# Revit family: 57_CRD_ME_Vita_H1C
name_source: partatom
category: Mechanical Equipment
units: mm (PartAtom-declared; Revit-internal decimal feet)

## family parameters
Always vertical = Yes
Classification = None
Cut with Voids When Loaded = Yes
Part Type = Normal
Room Calculation Point = Yes
Round Connector Dimension = Use Diameter
Shared = No
Work Plane-Based = Yes

## types (1)
- 1320  x 485 x 142
    Default Elevation = 1219 mm
    Description = ClimaRad Sensa H2X ventilatie-unit
    Manufacturer = ClimaRad
    Model = Sensa H2X
    bk_ril = 305 mm  [stored 1.00066 ft]
    borstwering = 465 mm  [stored 1.52559 ft]
    diepte = 270 mm  [stored 0.885827 ft]
    diepte_achterpaneel = 70 mm  [stored 0.229659 ft]
    diepte_ril = 6 mm  [stored 0.019685 ft]
    hart_doorvoer_tov_ok_kast = 345 mm  [stored 1.13189 ft]
    hart_wcd_tov_vloerpeil = 365 mm  [stored 1.19751 ft]
    hoh_ventilatie_doorvoeren = 1098 mm  [stored 3.60236 ft]
    hoogte = 445 mm  [stored 1.45997 ft]
    hoogte_ril = 6 mm  [stored 0.019685 ft]
    lengte = 1530 mm  [stored 5.01969 ft]
    lengte_achterpaneel = 1480 mm  [stored 4.85564 ft]
    positie_wcd_uit_hart_unit = 676 mm  [stored 2.21785 ft]
    ruimte_onder_unit = 20 mm  [stored 0.0656168 ft]
    schacht = Yes
    voltage = 230 V

note: [stored X ft] marks values corroborated as IEEE doubles in the binary element streams (Revit-internal decimal feet)

## geometry (parser evidence)
native form markers: Sweep x9
no freeform markers — native parametric forms only
